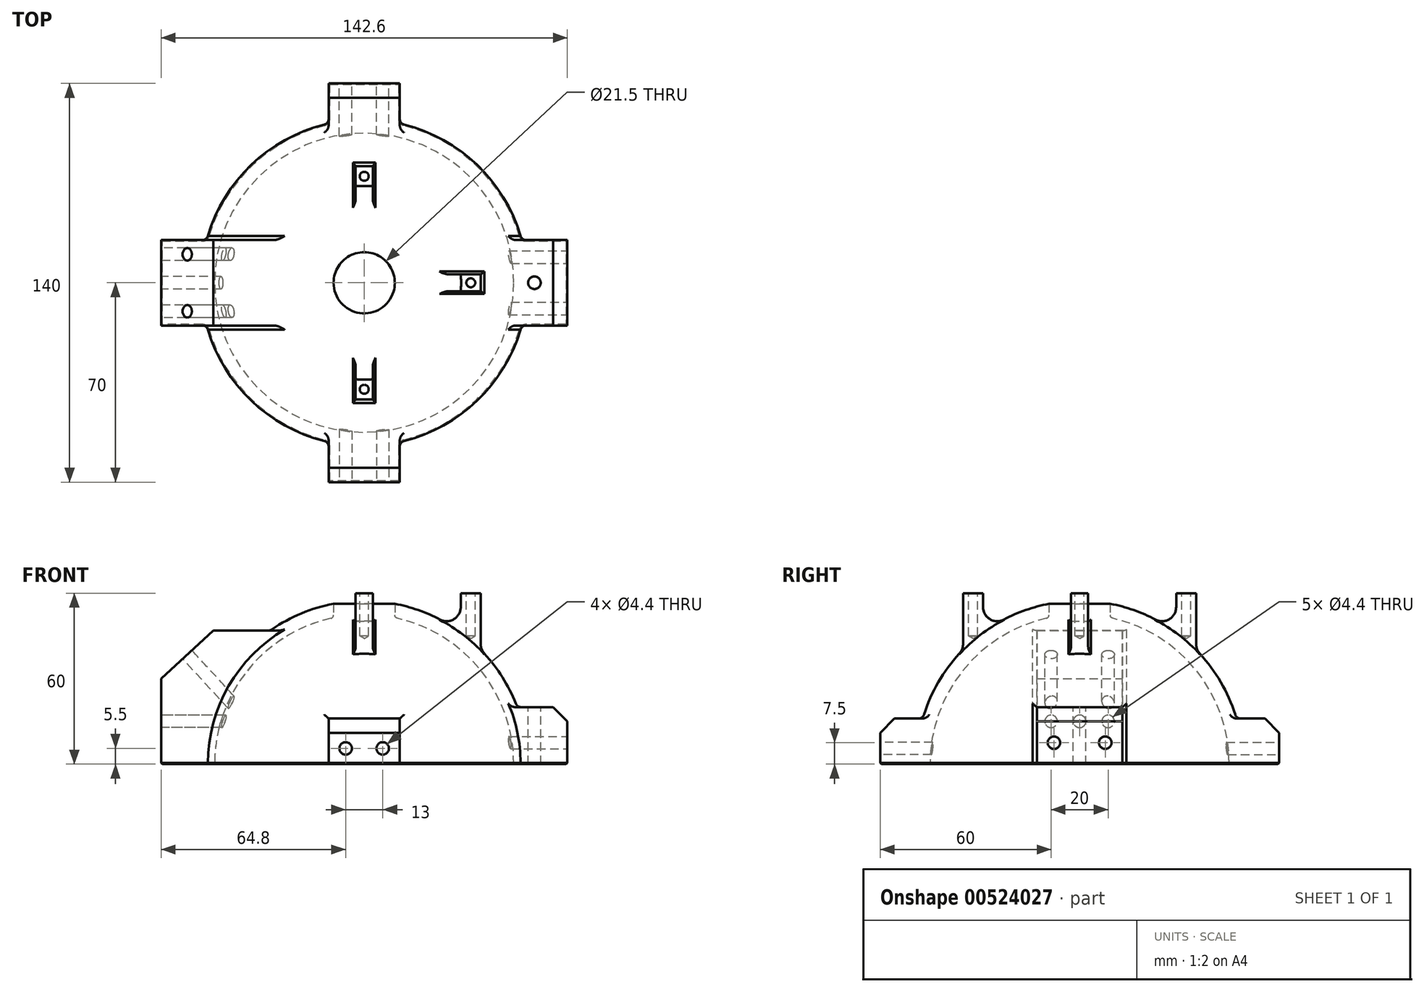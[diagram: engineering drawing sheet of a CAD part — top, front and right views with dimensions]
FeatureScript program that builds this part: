
annotation { "Feature Type Name" : "Feature", "Feature Type Description" : "" }
export const myFeature = defineFeature(function(context is Context, id is Id, definition is map)
    precondition{}
    {
        {
            var Q0;
            Q0=qCreatedBy(makeId("Front.planeOp"),FACE);
            var sketch = newSketch(context, id + "F0", { "sketchPlane" : qUnion([Q0])});
            skArc(sketch, "E0", {"start": v(52.5, 0) * mm, "mid": v(0, 52.5) * mm, "end": v(-52.5, 0) * mm});
            skLineSegment(sketch, "E1", {"start": v(-52.5, 0) * mm, "end": v(52.5, 0) * mm});
            skArc(sketch, "E2.0", {"start": v(57.3, 0) * mm, "mid": v(0, 57.3) * mm, "end": v(-57.3, 0) * mm});
            skLineSegment(sketch, "E3", {"start": v(-57.3, 0) * mm, "end": v(-52.5, 0) * mm});
            skLineSegment(sketch, "E4", {"start": v(52.5, 0) * mm, "end": v(57.3, 0) * mm});
            skLineSegment(sketch, "E5", {"start": v(-57.3, 0) * mm, "end": v(-71.3, 0) * mm});
            skLineSegment(sketch, "E6", {"start": v(-71.3, 0) * mm, "end": v(-71.3, 30) * mm});
            skLineSegment(sketch, "E7", {"start": v(-71.3, 30) * mm, "end": v(-52.9, 46.92) * mm});
            skLineSegment(sketch, "E8", {"start": v(-52.9, 46.92) * mm, "end": v(-32.9, 46.92) * mm});
            skLineSegment(sketch, "E9", {"start": v(0, 0) * mm, "end": v(0, 57.3) * mm});
            skLineSegment(sketch, "E10", {"start": v(-32.9, 46.92) * mm, "end": v(-23.56, 46.92) * mm});
            skLineSegment(sketch, "E11.bottom", {"start": v(10.75, 49.8) * mm, "end": v(-10.75, 49.8) * mm});
            skLineSegment(sketch, "E11.top", {"start": v(10.75, 64.8) * mm, "end": v(-10.75, 64.8) * mm});
            skLineSegment(sketch, "E11.left", {"start": v(10.75, 49.8) * mm, "end": v(10.75, 64.8) * mm});
            skLineSegment(sketch, "E11.right", {"start": v(-10.75, 49.8) * mm, "end": v(-10.75, 64.8) * mm});
            skPoint(sketch, "E11.middle", {"position": v(0, 57.3) * mm});
            skLineSegment(sketch, "E12", {"start": v(57.3, 0) * mm, "end": v(71.3, 0) * mm});
            skLineSegment(sketch, "E13", {"start": v(71.3, 0) * mm, "end": v(71.3, 20) * mm});
            skLineSegment(sketch, "E14", {"start": v(71.3, 20) * mm, "end": v(48.54, 20) * mm});
            skSolve(sketch);
        }
        {
            var Q0;
            {var subQ0=sQuery(id+"F0.wireOp",EDGE,"E4");Q0=makeQuery(id+"F0.imprint","IMPRINT",FACE,{"disambiguationData":[TD([[makeQuery(id+"F0.imprint","IMPRINT",EDGE,{"derivedFrom":subQ0}),1.0]])]});}
            var Q1;
            {var subQ0=sQuery(id+"F0.wireOp",EDGE,"E14");var subQ1=sQuery(id+"F0.wireOp",EDGE,"E0");var subQ2=makeQuery(id+"F0.imprint","INTERSECT",VERTEX,{"derivedFrom":[subQ1,subQ0]});Q1=makeQuery(id+"F0.imprint","IMPRINT",FACE,{"disambiguationData":[TD([[makeQuery(id+"F0.imprint","IMPRINT",EDGE,{"disambiguationData":[TD([[subQ2,-1.0]])],"derivedFrom":subQ1}),-1.0]])]});}
            var Q2;
            Q2=sQuery(id+"F0.wireOp",EDGE,"E9");
            revolve(context, id + "F1", {"entities" : qUnion([Q0, Q1]), "axis" : qUnion([Q2]), "revolveType" : RevolveType.FULL});
        }
        {
            var Q0;
            {var subQ0=sQuery(id+"F0.wireOp",EDGE,"E5");Q0=makeQuery(id+"F0.imprint","IMPRINT",FACE,{"disambiguationData":[TD([[makeQuery(id+"F0.imprint","IMPRINT",EDGE,{"derivedFrom":subQ0}),-1.0]])]});}
            var Q1;
            {var subQ0=sQuery(id+"F0.wireOp",EDGE,"E3");Q1=makeQuery(id+"F0.imprint","IMPRINT",FACE,{"disambiguationData":[TD([[makeQuery(id+"F0.imprint","IMPRINT",EDGE,{"derivedFrom":subQ0}),1.0]])]});}
            var Q2;
            {var subQ0=sQuery(id+"F0.wireOp",EDGE,"E4");Q2=makeQuery(id+"F0.imprint","IMPRINT",FACE,{"disambiguationData":[TD([[makeQuery(id+"F0.imprint","IMPRINT",EDGE,{"derivedFrom":subQ0}),1.0]])]});}
            var Q3;
            {var subQ0=sQuery(id+"F0.wireOp",EDGE,"E12");Q3=makeQuery(id+"F0.imprint","IMPRINT",FACE,{"disambiguationData":[TD([[makeQuery(id+"F0.imprint","IMPRINT",EDGE,{"derivedFrom":subQ0}),1.0]])]});}
            extrude(context, id + "F2", {"entities" : qUnion([Q0, Q1, Q2, Q3]), "operationType" : NewBodyOperationType.ADD, "endBound" : BoundingType.SYMMETRIC, "depth" : 30 * mm, "offsetDistance" : 25 * mm});
        }
        {
            var Q0;
            Q0=qCreatedBy(makeId("Right.planeOp"),FACE);
            var sketch = newSketch(context, id + "F3", { "sketchPlane" : qUnion([Q0])});
            skLineSegment(sketch, "E15.bottom", {"start": v(-70, 0) * mm, "end": v(70, 0) * mm});
            skLineSegment(sketch, "E15.top", {"start": v(-70, 16) * mm, "end": v(70, 16) * mm});
            skLineSegment(sketch, "E15.left", {"start": v(-70, 0) * mm, "end": v(-70, 16) * mm});
            skLineSegment(sketch, "E15.right", {"start": v(70, 0) * mm, "end": v(70, 16) * mm});
            skPoint(sketch, "E15.middle", {"position": v(0, 8) * mm});
            skArc(sketch, "E16", {"start": v(-10.75, 56.28) * mm, "mid": v(-44.15, 36.52) * mm, "end": v(-57.3, 0) * mm});
            skArc(sketch, "E17", {"start": v(57.3, 0) * mm, "mid": v(44.15, 36.52) * mm, "end": v(10.75, 56.28) * mm});
            skArc(sketch, "E18", {"start": v(-10.75, 51.39) * mm, "mid": v(-40.75, 33.1) * mm, "end": v(-52.5, 0) * mm});
            skArc(sketch, "E19", {"start": v(52.5, 0) * mm, "mid": v(40.75, 33.1) * mm, "end": v(10.75, 51.39) * mm});
            skSolve(sketch);
        }
        {
            var Q0;
            {var subQ0=sQuery(id+"F3.wireOp",EDGE,"E16");var subQ1=sQuery(id+"F3.wireOp",EDGE,"E15.bottom");var subQ2=makeQuery(id+"F3.imprint","INTERSECT",VERTEX,{"derivedFrom":[subQ1,subQ0]});Q0=makeQuery(id+"F3.imprint","IMPRINT",FACE,{"disambiguationData":[TD([[makeQuery(id+"F3.imprint","IMPRINT",EDGE,{"disambiguationData":[TD([[subQ2,-1.0]])],"derivedFrom":subQ1}),1.0]])]});}
            var Q1;
            {var subQ0=sQuery(id+"F3.wireOp",EDGE,"E15.left");Q1=makeQuery(id+"F3.imprint","IMPRINT",FACE,{"disambiguationData":[TD([[makeQuery(id+"F3.imprint","IMPRINT",EDGE,{"derivedFrom":subQ0}),-1.0]])]});}
            var Q2;
            {var subQ0=sQuery(id+"F3.wireOp",EDGE,"E17");var subQ1=sQuery(id+"F3.wireOp",EDGE,"E15.bottom");var subQ2=makeQuery(id+"F3.imprint","INTERSECT",VERTEX,{"derivedFrom":[subQ1,subQ0]});Q2=makeQuery(id+"F3.imprint","IMPRINT",FACE,{"disambiguationData":[TD([[makeQuery(id+"F3.imprint","IMPRINT",EDGE,{"disambiguationData":[TD([[subQ2,1.0]])],"derivedFrom":subQ1}),1.0]])]});}
            var Q3;
            {var subQ0=sQuery(id+"F3.wireOp",EDGE,"E15.right");Q3=makeQuery(id+"F3.imprint","IMPRINT",FACE,{"disambiguationData":[TD([[makeQuery(id+"F3.imprint","IMPRINT",EDGE,{"derivedFrom":subQ0}),1.0]])]});}
            extrude(context, id + "F4", {"entities" : qUnion([Q0, Q1, Q2, Q3]), "operationType" : NewBodyOperationType.ADD, "endBound" : BoundingType.SYMMETRIC, "depth" : 25 * mm, "offsetDistance" : 25 * mm});
        }
        {
            var Q0;
            Q0=makeQuery(id+"F4.opExtrude","SWEPT_EDGE",EDGE,{"disambiguationData":[OSD([sQuery(id+"F3.wireOp",EDGE,"E15.top"),sQuery(id+"F3.wireOp",EDGE,"E15.left")])]});
            var Q1;
            Q1=makeQuery(id+"F2.opExtrude","SWEPT_EDGE",EDGE,{"disambiguationData":[OSD([sQuery(id+"F0.wireOp",EDGE,"E13"),sQuery(id+"F0.wireOp",EDGE,"E14")])]});
            var Q2;
            Q2=makeQuery(id+"F4.opExtrude","SWEPT_EDGE",EDGE,{"disambiguationData":[OSD([sQuery(id+"F3.wireOp",EDGE,"E15.top"),sQuery(id+"F3.wireOp",EDGE,"E15.right")])]});
            chamfer(context, id + "F5", {"entities" : qUnion([Q0, Q1, Q2]), "width" : 5 * mm, "tangentPropagation" : true});
        }
        {
            var Q0;
            Q0=makeQuery(id+"F1.opRevolve","SWEPT_EDGE",EDGE,{"disambiguationData":[OSD([sQuery(id+"F0.wireOp",EDGE,"E0"),sQuery(id+"F0.wireOp",EDGE,"E11.left")])]});
            fillet(context, id + "F6", {"entities" : qUnion([Q0]), "radius" : 1.2 * mm, "tangentPropagation" : true, "allowEdgeOverflow" : false});
        }
        {
            var Q0;
            Q0=makeQuery(id+"F2.boolean.opBoolean","INTERSECT",EDGE,{"derivedFrom":[makeQuery(id+"F1.opRevolve","SWEPT_FACE",FACE,{"disambiguationData":[OSD([sQuery(id+"F0.wireOp",EDGE,"E2.0")])]}),makeQuery(id+"F2.opExtrude","CAP_FACE",FACE,{"disambiguationData":[OSD([sQuery(id+"F0.wireOp",EDGE,"E0"),sQuery(id+"F0.wireOp",EDGE,"E3"),sQuery(id+"F0.wireOp",EDGE,"E5"),sQuery(id+"F0.wireOp",EDGE,"E6"),sQuery(id+"F0.wireOp",EDGE,"E7"),sQuery(id+"F0.wireOp",EDGE,"E8"),sQuery(id+"F0.wireOp",EDGE,"E10")])],"isStart":false})]});
            var Q1;
            Q1=makeQuery(id+"F2.boolean.opBoolean","INTERSECT",EDGE,{"derivedFrom":[makeQuery(id+"F1.opRevolve","SWEPT_FACE",FACE,{"disambiguationData":[OSD([sQuery(id+"F0.wireOp",EDGE,"E2.0")])]}),makeQuery(id+"F2.opExtrude","CAP_FACE",FACE,{"disambiguationData":[OSD([sQuery(id+"F0.wireOp",EDGE,"E0"),sQuery(id+"F0.wireOp",EDGE,"E4"),sQuery(id+"F0.wireOp",EDGE,"E12"),sQuery(id+"F0.wireOp",EDGE,"E13"),sQuery(id+"F0.wireOp",EDGE,"E14")])],"isStart":false})]});
            var Q2;
            Q2=makeQuery(id+"F4.boolean.opBoolean","INTERSECT",EDGE,{"derivedFrom":[makeQuery(id+"F1.opRevolve","SWEPT_FACE",FACE,{"disambiguationData":[OSD([sQuery(id+"F0.wireOp",EDGE,"E2.0")])]}),makeQuery(id+"F4.opExtrude","CAP_FACE",FACE,{"disambiguationData":[OSD([sQuery(id+"F3.wireOp",EDGE,"E15.bottom"),sQuery(id+"F3.wireOp",EDGE,"E15.top"),sQuery(id+"F3.wireOp",EDGE,"E15.left"),sQuery(id+"F3.wireOp",EDGE,"E18")])],"isStart":false})]});
            var Q3;
            Q3=makeQuery(id+"F4.boolean.opBoolean","INTERSECT",EDGE,{"derivedFrom":[makeQuery(id+"F1.opRevolve","SWEPT_FACE",FACE,{"disambiguationData":[OSD([sQuery(id+"F0.wireOp",EDGE,"E2.0")])]}),makeQuery(id+"F4.opExtrude","CAP_FACE",FACE,{"disambiguationData":[OSD([sQuery(id+"F3.wireOp",EDGE,"E15.bottom"),sQuery(id+"F3.wireOp",EDGE,"E15.top"),sQuery(id+"F3.wireOp",EDGE,"E15.left"),sQuery(id+"F3.wireOp",EDGE,"E18")])],"isStart":true})]});
            var Q4;
            Q4=makeQuery(id+"F2.boolean.opBoolean","INTERSECT",EDGE,{"derivedFrom":[makeQuery(id+"F1.opRevolve","SWEPT_FACE",FACE,{"disambiguationData":[OSD([sQuery(id+"F0.wireOp",EDGE,"E2.0")])]}),makeQuery(id+"F2.opExtrude","CAP_FACE",FACE,{"disambiguationData":[OSD([sQuery(id+"F0.wireOp",EDGE,"E0"),sQuery(id+"F0.wireOp",EDGE,"E3"),sQuery(id+"F0.wireOp",EDGE,"E5"),sQuery(id+"F0.wireOp",EDGE,"E6"),sQuery(id+"F0.wireOp",EDGE,"E7"),sQuery(id+"F0.wireOp",EDGE,"E8"),sQuery(id+"F0.wireOp",EDGE,"E10")])],"isStart":true})]});
            var Q5;
            Q5=makeQuery(id+"F4.boolean.opBoolean","INTERSECT",EDGE,{"derivedFrom":[makeQuery(id+"F1.opRevolve","SWEPT_FACE",FACE,{"disambiguationData":[OSD([sQuery(id+"F0.wireOp",EDGE,"E2.0")])]}),makeQuery(id+"F4.opExtrude","CAP_FACE",FACE,{"disambiguationData":[OSD([sQuery(id+"F3.wireOp",EDGE,"E15.bottom"),sQuery(id+"F3.wireOp",EDGE,"E15.top"),sQuery(id+"F3.wireOp",EDGE,"E15.right"),sQuery(id+"F3.wireOp",EDGE,"E19")])],"isStart":true})]});
            var Q6;
            Q6=makeQuery(id+"F4.boolean.opBoolean","INTERSECT",EDGE,{"derivedFrom":[makeQuery(id+"F1.opRevolve","SWEPT_FACE",FACE,{"disambiguationData":[OSD([sQuery(id+"F0.wireOp",EDGE,"E2.0")])]}),makeQuery(id+"F4.opExtrude","CAP_FACE",FACE,{"disambiguationData":[OSD([sQuery(id+"F3.wireOp",EDGE,"E15.bottom"),sQuery(id+"F3.wireOp",EDGE,"E15.top"),sQuery(id+"F3.wireOp",EDGE,"E15.right"),sQuery(id+"F3.wireOp",EDGE,"E19")])],"isStart":false})]});
            var Q7;
            Q7=makeQuery(id+"F2.boolean.opBoolean","INTERSECT",EDGE,{"derivedFrom":[makeQuery(id+"F1.opRevolve","SWEPT_FACE",FACE,{"disambiguationData":[OSD([sQuery(id+"F0.wireOp",EDGE,"E2.0")])]}),makeQuery(id+"F2.opExtrude","SWEPT_FACE",FACE,{"disambiguationData":[OSD([sQuery(id+"F0.wireOp",EDGE,"E8"),sQuery(id+"F0.wireOp",EDGE,"E10")])]})]});
            var Q8;
            {var subQ0=sQuery(id+"F3.wireOp",EDGE,"E15.top");var subQ1=makeQuery(id+"F3.imprint","INTERSECT",VERTEX,{"derivedFrom":[subQ0,sQuery(id+"F3.wireOp",EDGE,"E16")]});Q8=makeQuery(id+"F4.boolean.opBoolean","INTERSECT",EDGE,{"derivedFrom":[makeQuery(id+"F1.opRevolve","SWEPT_FACE",FACE,{"disambiguationData":[OSD([sQuery(id+"F0.wireOp",EDGE,"E2.0")])]}),makeQuery(id+"F4.opExtrude","SWEPT_FACE",FACE,{"disambiguationData":[OSD([subQ0]),TDD([makeQuery(id+"F3.imprint","IMPRINT",EDGE,{"disambiguationData":[TD([[makeQuery(id+"F3.imprint","INTERSECT",VERTEX,{"derivedFrom":[subQ0,sQuery(id+"F3.wireOp",EDGE,"E15.left")]}),-1.0]])],"derivedFrom":subQ0}),makeQuery(id+"F3.imprint","IMPRINT",EDGE,{"disambiguationData":[TD([[subQ1,-1.0]])],"derivedFrom":subQ0})])]})]});}
            var Q9;
            Q9=makeQuery(id+"F2.boolean.opBoolean","INTERSECT",EDGE,{"derivedFrom":[makeQuery(id+"F1.opRevolve","SWEPT_FACE",FACE,{"disambiguationData":[OSD([sQuery(id+"F0.wireOp",EDGE,"E2.0")])]}),makeQuery(id+"F2.opExtrude","CAP_FACE",FACE,{"disambiguationData":[OSD([sQuery(id+"F0.wireOp",EDGE,"E0"),sQuery(id+"F0.wireOp",EDGE,"E4"),sQuery(id+"F0.wireOp",EDGE,"E12"),sQuery(id+"F0.wireOp",EDGE,"E13"),sQuery(id+"F0.wireOp",EDGE,"E14")])],"isStart":true})]});
            var Q10;
            Q10=makeQuery(id+"F2.boolean.opBoolean","INTERSECT",EDGE,{"derivedFrom":[makeQuery(id+"F1.opRevolve","SWEPT_FACE",FACE,{"disambiguationData":[OSD([sQuery(id+"F0.wireOp",EDGE,"E2.0")])]}),makeQuery(id+"F2.opExtrude","SWEPT_FACE",FACE,{"disambiguationData":[OSD([sQuery(id+"F0.wireOp",EDGE,"E14")])]})]});
            var Q11;
            {var subQ0=sQuery(id+"F3.wireOp",EDGE,"E15.top");Q11=makeQuery(id+"F4.boolean.opBoolean","INTERSECT",EDGE,{"derivedFrom":[makeQuery(id+"F1.opRevolve","SWEPT_FACE",FACE,{"disambiguationData":[OSD([sQuery(id+"F0.wireOp",EDGE,"E2.0")])]}),makeQuery(id+"F4.opExtrude","SWEPT_FACE",FACE,{"disambiguationData":[OSD([subQ0]),TDD([makeQuery(id+"F3.imprint","IMPRINT",EDGE,{"disambiguationData":[TD([[makeQuery(id+"F3.imprint","INTERSECT",VERTEX,{"derivedFrom":[subQ0,sQuery(id+"F3.wireOp",EDGE,"E19")]}),-1.0]])],"derivedFrom":subQ0}),makeQuery(id+"F3.imprint","IMPRINT",EDGE,{"disambiguationData":[TD([[makeQuery(id+"F3.imprint","INTERSECT",VERTEX,{"derivedFrom":[subQ0,sQuery(id+"F3.wireOp",EDGE,"E15.right")]}),1.0]])],"derivedFrom":subQ0})])]})]});}
            fillet(context, id + "F7", {"entities" : qUnion([Q0, Q1, Q2, Q3, Q4, Q5, Q6, Q7, Q8, Q9, Q10, Q11]), "radius" : 2 * mm, "tangentPropagation" : true, "allowEdgeOverflow" : false});
        }
        {
            var Q0;
            Q0=makeQuery(id+"F2.opExtrude","SWEPT_FACE",FACE,{"disambiguationData":[OSD([sQuery(id+"F0.wireOp",EDGE,"E6")])]});
            var sketch = newSketch(context, id + "F8", { "sketchPlane" : qUnion([Q0])});
            skPoint(sketch, "E20", {"position": v(-10, 15) * mm});
            skPoint(sketch, "E20.positionSnap0", {"position": v(-15, 15) * mm});
            skPoint(sketch, "E21", {"position": v(10, 15) * mm});
            skPoint(sketch, "E22", {"position": v(0, 15) * mm});
            skSolve(sketch);
        }
        {
            var Q0;
            Q0=makeQuery(id+"F2.opExtrude","SWEPT_FACE",FACE,{"disambiguationData":[OSD([sQuery(id+"F0.wireOp",EDGE,"E7")])]});
            var sketch = newSketch(context, id + "F9", { "sketchPlane" : qUnion([Q0])});
            skPoint(sketch, "E23", {"position": v(-19.7, 10) * mm});
            skPoint(sketch, "E23.positionSnap0", {"position": v(-19.7, 15) * mm});
            skPoint(sketch, "E24", {"position": v(-19.7, -10) * mm});
            skPoint(sketch, "E25", {"position": v(-19.7, 0) * mm});
            skSolve(sketch);
        }
        {
            var Q0;
            Q0=makeQuery(id+"F4.opExtrude","SWEPT_FACE",FACE,{"disambiguationData":[OSD([sQuery(id+"F3.wireOp",EDGE,"E15.right")])]});
            var sketch = newSketch(context, id + "F10", { "sketchPlane" : qUnion([Q0])});
            skPoint(sketch, "E26", {"position": v(-6.5, 5.5) * mm});
            skPoint(sketch, "E26.positionSnap0", {"position": v(0, 11) * mm});
            skPoint(sketch, "E26.positionSnap1", {"position": v(12.5, 5.5) * mm});
            skPoint(sketch, "E27", {"position": v(6.5, 5.5) * mm});
            skSolve(sketch);
        }
        {
            var Q0;
            Q0=makeQuery(id+"F4.opExtrude","SWEPT_FACE",FACE,{"disambiguationData":[OSD([sQuery(id+"F3.wireOp",EDGE,"E15.left")])]});
            var sketch = newSketch(context, id + "F11", { "sketchPlane" : qUnion([Q0])});
            skPoint(sketch, "E28", {"position": v(6.5, 5.5) * mm});
            skPoint(sketch, "E28.positionSnap0", {"position": v(12.5, 5.5) * mm});
            skPoint(sketch, "E28.positionSnap1", {"position": v(0, 11) * mm});
            skPoint(sketch, "E29", {"position": v(-6.5, 5.5) * mm});
            skSolve(sketch);
        }
        {
            var Q0;
            Q0=makeQuery(id+"F2.opExtrude","SWEPT_FACE",FACE,{"disambiguationData":[OSD([sQuery(id+"F0.wireOp",EDGE,"E13")])]});
            var sketch = newSketch(context, id + "F12", { "sketchPlane" : qUnion([Q0])});
            skPoint(sketch, "E30", {"position": v(-9, 7.5) * mm});
            skPoint(sketch, "E30.positionSnap0", {"position": v(-15, 7.5) * mm});
            skPoint(sketch, "E31", {"position": v(9, 7.5) * mm});
            skPoint(sketch, "E31.positionSnap0", {"position": v(15, 7.5) * mm});
            skSolve(sketch);
        }
        {
            var Q0;
            Q0=makeQuery(id+"F2.opExtrude","SWEPT_FACE",FACE,{"disambiguationData":[OSD([sQuery(id+"F0.wireOp",EDGE,"E14")])]});
            var sketch = newSketch(context, id + "F13", { "sketchPlane" : qUnion([Q0])});
            skPoint(sketch, "E32", {"position": v(59.74, 0) * mm});
            skPoint(sketch, "E32.positionSnap0", {"position": v(59.74, 15) * mm});
            skPoint(sketch, "E32.positionSnap1", {"position": v(66.3, 0) * mm});
            skSolve(sketch);
        }
        {
            var Q0;
            Q0=sQuery(id+"F9.wireOp",VERTEX,"E23");
            var Q1;
            Q1=sQuery(id+"F9.wireOp",VERTEX,"E24");
            var Q2;
            Q2=sQuery(id+"F8.wireOp",VERTEX,"E20");
            var Q3;
            Q3=sQuery(id+"F8.wireOp",VERTEX,"E22");
            var Q4;
            Q4=sQuery(id+"F8.wireOp",VERTEX,"E21");
            var Q5;
            Q5=sQuery(id+"F11.wireOp",VERTEX,"E28");
            var Q6;
            Q6=sQuery(id+"F10.wireOp",VERTEX,"E26");
            var Q7;
            Q7=sQuery(id+"F12.wireOp",VERTEX,"E30");
            var Q8;
            Q8=sQuery(id+"F12.wireOp",VERTEX,"E31");
            var Q9;
            Q9=sQuery(id+"F13.wireOp",VERTEX,"E32");
            var Q10;
            Q10=sQuery(id+"F10.wireOp",VERTEX,"E27");
            var Q11;
            Q11=sQuery(id+"F11.wireOp",VERTEX,"E29");
            var Q12;
            Q12=makeQuery(id+"F1.opRevolve","SWEPT_BODY",BODY,{"disambiguationData":[OSD([sQuery(id+"F0.wireOp",EDGE,"E0"),sQuery(id+"F0.wireOp",EDGE,"E2.0"),sQuery(id+"F0.wireOp",EDGE,"E4"),sQuery(id+"F0.wireOp",EDGE,"E11.left")])]});
            hole(context, id + "F14", {"style" : HoleStyle.SIMPLE, "endStyle" : HoleEndStyle.BLIND, "standardTappedOrClearance" : lookupTablePath({ "standard" : "ISO", "fit" : "Normal", "size" : "M4", "type" : "Clearance" }), "standardBlindInLast" : lookupTablePath({ "fit" : "Standard", "standard" : "ISO", "size" : "M4", "type" : "Clearance" }), "holeDiameter" : 4.4 * mm, "holeDepth" : 40 * mm, "isTappedThrough" : true, "tappedDepth" : 12 * mm, "tapClearance" : 3, "locations" : qUnion([Q0, Q1, Q2, Q3, Q4, Q5, Q6, Q7, Q8, Q9, Q10, Q11]), "scope" : qUnion([Q12])});
        }
        {
            var Q0;
            {var subQ0=sQuery(id+"F3.wireOp",EDGE,"E15.bottom");var subQ1=makeQuery(id+"F3.imprint","INTERSECT",VERTEX,{"derivedFrom":[subQ0,sQuery(id+"F3.wireOp",EDGE,"E17")]});var subQ2=makeQuery(id+"F3.imprint","INTERSECT",VERTEX,{"derivedFrom":[subQ0,sQuery(id+"F3.wireOp",EDGE,"E16")]});var subQ3=sQuery(id+"F3.wireOp",EDGE,"E18");var subQ4=sQuery(id+"F3.wireOp",EDGE,"E15.left");var subQ5=sQuery(id+"F0.wireOp",EDGE,"E4");Q0=makeQuery(id+"F7.opFillet","BLEND_EDGE",EDGE,{"blendedFrom":[makeQuery(id+"F4.boolean.opBoolean","INTERSECT",EDGE,{"derivedFrom":[makeQuery(id+"F1.opRevolve","SWEPT_FACE",FACE,{"disambiguationData":[OSD([sQuery(id+"F0.wireOp",EDGE,"E2.0")])]}),makeQuery(id+"F4.opExtrude","CAP_FACE",FACE,{"disambiguationData":[OSD([subQ0,sQuery(id+"F3.wireOp",EDGE,"E15.top"),subQ4,subQ3])],"isStart":false})]}),makeQuery(id+"F4.boolean.opBoolean","MERGE",FACE,{"derivedFrom":[makeQuery(id+"F2.boolean.opBoolean","MERGE",FACE,{"derivedFrom":[makeQuery(id+"F1.opRevolve","SWEPT_FACE",FACE,{"disambiguationData":[OSD([subQ5])]}),makeQuery(id+"F2.opExtrude","SWEPT_FACE",FACE,{"disambiguationData":[OSD([sQuery(id+"F0.wireOp",EDGE,"E3"),sQuery(id+"F0.wireOp",EDGE,"E5")])]}),makeQuery(id+"F2.opExtrude","SWEPT_FACE",FACE,{"disambiguationData":[OSD([subQ5,sQuery(id+"F0.wireOp",EDGE,"E12")])]})]}),makeQuery(id+"F4.opExtrude","SWEPT_FACE",FACE,{"disambiguationData":[OSD([subQ0]),TDD([makeQuery(id+"F3.imprint","IMPRINT",EDGE,{"disambiguationData":[TD([[makeQuery(id+"F3.imprint","INTERSECT",VERTEX,{"derivedFrom":[subQ0,subQ4]}),-1.0]])],"derivedFrom":subQ0}),makeQuery(id+"F3.imprint","IMPRINT",EDGE,{"disambiguationData":[TD([[subQ2,-1.0]])],"derivedFrom":subQ0})])]}),makeQuery(id+"F4.opExtrude","SWEPT_FACE",FACE,{"disambiguationData":[OSD([subQ0]),TDD([makeQuery(id+"F3.imprint","IMPRINT",EDGE,{"disambiguationData":[TD([[subQ1,1.0]])],"derivedFrom":subQ0}),makeQuery(id+"F3.imprint","IMPRINT",EDGE,{"disambiguationData":[TD([[makeQuery(id+"F3.imprint","INTERSECT",VERTEX,{"derivedFrom":[subQ0,sQuery(id+"F3.wireOp",EDGE,"E15.right")]}),1.0]])],"derivedFrom":subQ0})])]})]})],"blendedInto":[makeQuery(id+"F4.boolean.opBoolean","MERGE",FACE,{"derivedFrom":[makeQuery(id+"F2.boolean.opBoolean","MERGE",FACE,{"derivedFrom":[makeQuery(id+"F1.opRevolve","SWEPT_FACE",FACE,{"disambiguationData":[OSD([subQ5])]}),makeQuery(id+"F2.opExtrude","SWEPT_FACE",FACE,{"disambiguationData":[OSD([sQuery(id+"F0.wireOp",EDGE,"E3"),sQuery(id+"F0.wireOp",EDGE,"E5")])]}),makeQuery(id+"F2.opExtrude","SWEPT_FACE",FACE,{"disambiguationData":[OSD([subQ5,sQuery(id+"F0.wireOp",EDGE,"E12")])]})]}),makeQuery(id+"F4.opExtrude","SWEPT_FACE",FACE,{"disambiguationData":[OSD([subQ0]),TDD([makeQuery(id+"F3.imprint","IMPRINT",EDGE,{"disambiguationData":[TD([[makeQuery(id+"F3.imprint","INTERSECT",VERTEX,{"derivedFrom":[subQ0,subQ4]}),-1.0]])],"derivedFrom":subQ0}),makeQuery(id+"F3.imprint","IMPRINT",EDGE,{"disambiguationData":[TD([[subQ2,-1.0]])],"derivedFrom":subQ0})])]}),makeQuery(id+"F4.opExtrude","SWEPT_FACE",FACE,{"disambiguationData":[OSD([subQ0]),TDD([makeQuery(id+"F3.imprint","IMPRINT",EDGE,{"disambiguationData":[TD([[subQ1,1.0]])],"derivedFrom":subQ0}),makeQuery(id+"F3.imprint","IMPRINT",EDGE,{"disambiguationData":[TD([[makeQuery(id+"F3.imprint","INTERSECT",VERTEX,{"derivedFrom":[subQ0,sQuery(id+"F3.wireOp",EDGE,"E15.right")]}),1.0]])],"derivedFrom":subQ0})])]})]})]});}
            var Q1;
            {var subQ0=sQuery(id+"F3.wireOp",EDGE,"E15.bottom");var subQ1=makeQuery(id+"F3.imprint","INTERSECT",VERTEX,{"derivedFrom":[subQ0,sQuery(id+"F3.wireOp",EDGE,"E17")]});var subQ2=makeQuery(id+"F3.imprint","INTERSECT",VERTEX,{"derivedFrom":[subQ0,sQuery(id+"F3.wireOp",EDGE,"E16")]});var subQ3=sQuery(id+"F3.wireOp",EDGE,"E18");var subQ4=sQuery(id+"F3.wireOp",EDGE,"E15.left");var subQ5=sQuery(id+"F0.wireOp",EDGE,"E4");Q1=makeQuery(id+"F7.opFillet","BLEND_EDGE",EDGE,{"blendedFrom":[makeQuery(id+"F4.boolean.opBoolean","INTERSECT",EDGE,{"derivedFrom":[makeQuery(id+"F1.opRevolve","SWEPT_FACE",FACE,{"disambiguationData":[OSD([sQuery(id+"F0.wireOp",EDGE,"E2.0")])]}),makeQuery(id+"F4.opExtrude","CAP_FACE",FACE,{"disambiguationData":[OSD([subQ0,sQuery(id+"F3.wireOp",EDGE,"E15.top"),subQ4,subQ3])],"isStart":true})]}),makeQuery(id+"F4.boolean.opBoolean","MERGE",FACE,{"derivedFrom":[makeQuery(id+"F2.boolean.opBoolean","MERGE",FACE,{"derivedFrom":[makeQuery(id+"F1.opRevolve","SWEPT_FACE",FACE,{"disambiguationData":[OSD([subQ5])]}),makeQuery(id+"F2.opExtrude","SWEPT_FACE",FACE,{"disambiguationData":[OSD([sQuery(id+"F0.wireOp",EDGE,"E3"),sQuery(id+"F0.wireOp",EDGE,"E5")])]}),makeQuery(id+"F2.opExtrude","SWEPT_FACE",FACE,{"disambiguationData":[OSD([subQ5,sQuery(id+"F0.wireOp",EDGE,"E12")])]})]}),makeQuery(id+"F4.opExtrude","SWEPT_FACE",FACE,{"disambiguationData":[OSD([subQ0]),TDD([makeQuery(id+"F3.imprint","IMPRINT",EDGE,{"disambiguationData":[TD([[makeQuery(id+"F3.imprint","INTERSECT",VERTEX,{"derivedFrom":[subQ0,subQ4]}),-1.0]])],"derivedFrom":subQ0}),makeQuery(id+"F3.imprint","IMPRINT",EDGE,{"disambiguationData":[TD([[subQ2,-1.0]])],"derivedFrom":subQ0})])]}),makeQuery(id+"F4.opExtrude","SWEPT_FACE",FACE,{"disambiguationData":[OSD([subQ0]),TDD([makeQuery(id+"F3.imprint","IMPRINT",EDGE,{"disambiguationData":[TD([[subQ1,1.0]])],"derivedFrom":subQ0}),makeQuery(id+"F3.imprint","IMPRINT",EDGE,{"disambiguationData":[TD([[makeQuery(id+"F3.imprint","INTERSECT",VERTEX,{"derivedFrom":[subQ0,sQuery(id+"F3.wireOp",EDGE,"E15.right")]}),1.0]])],"derivedFrom":subQ0})])]})]})],"blendedInto":[makeQuery(id+"F4.boolean.opBoolean","MERGE",FACE,{"derivedFrom":[makeQuery(id+"F2.boolean.opBoolean","MERGE",FACE,{"derivedFrom":[makeQuery(id+"F1.opRevolve","SWEPT_FACE",FACE,{"disambiguationData":[OSD([subQ5])]}),makeQuery(id+"F2.opExtrude","SWEPT_FACE",FACE,{"disambiguationData":[OSD([sQuery(id+"F0.wireOp",EDGE,"E3"),sQuery(id+"F0.wireOp",EDGE,"E5")])]}),makeQuery(id+"F2.opExtrude","SWEPT_FACE",FACE,{"disambiguationData":[OSD([subQ5,sQuery(id+"F0.wireOp",EDGE,"E12")])]})]}),makeQuery(id+"F4.opExtrude","SWEPT_FACE",FACE,{"disambiguationData":[OSD([subQ0]),TDD([makeQuery(id+"F3.imprint","IMPRINT",EDGE,{"disambiguationData":[TD([[makeQuery(id+"F3.imprint","INTERSECT",VERTEX,{"derivedFrom":[subQ0,subQ4]}),-1.0]])],"derivedFrom":subQ0}),makeQuery(id+"F3.imprint","IMPRINT",EDGE,{"disambiguationData":[TD([[subQ2,-1.0]])],"derivedFrom":subQ0})])]}),makeQuery(id+"F4.opExtrude","SWEPT_FACE",FACE,{"disambiguationData":[OSD([subQ0]),TDD([makeQuery(id+"F3.imprint","IMPRINT",EDGE,{"disambiguationData":[TD([[subQ1,1.0]])],"derivedFrom":subQ0}),makeQuery(id+"F3.imprint","IMPRINT",EDGE,{"disambiguationData":[TD([[makeQuery(id+"F3.imprint","INTERSECT",VERTEX,{"derivedFrom":[subQ0,sQuery(id+"F3.wireOp",EDGE,"E15.right")]}),1.0]])],"derivedFrom":subQ0})])]})]})]});}
            var Q2;
            {var subQ0=sQuery(id+"F3.wireOp",EDGE,"E15.bottom");var subQ1=makeQuery(id+"F3.imprint","INTERSECT",VERTEX,{"derivedFrom":[subQ0,sQuery(id+"F3.wireOp",EDGE,"E17")]});var subQ2=makeQuery(id+"F3.imprint","INTERSECT",VERTEX,{"derivedFrom":[subQ0,sQuery(id+"F3.wireOp",EDGE,"E16")]});var subQ3=sQuery(id+"F0.wireOp",EDGE,"E12");var subQ4=sQuery(id+"F0.wireOp",EDGE,"E4");Q2=makeQuery(id+"F7.opFillet","BLEND_EDGE",EDGE,{"blendedFrom":[makeQuery(id+"F2.boolean.opBoolean","INTERSECT",EDGE,{"derivedFrom":[makeQuery(id+"F1.opRevolve","SWEPT_FACE",FACE,{"disambiguationData":[OSD([sQuery(id+"F0.wireOp",EDGE,"E2.0")])]}),makeQuery(id+"F2.opExtrude","CAP_FACE",FACE,{"disambiguationData":[OSD([sQuery(id+"F0.wireOp",EDGE,"E0"),subQ4,subQ3,sQuery(id+"F0.wireOp",EDGE,"E13"),sQuery(id+"F0.wireOp",EDGE,"E14")])],"isStart":true})]}),makeQuery(id+"F4.boolean.opBoolean","MERGE",FACE,{"derivedFrom":[makeQuery(id+"F2.boolean.opBoolean","MERGE",FACE,{"derivedFrom":[makeQuery(id+"F1.opRevolve","SWEPT_FACE",FACE,{"disambiguationData":[OSD([subQ4])]}),makeQuery(id+"F2.opExtrude","SWEPT_FACE",FACE,{"disambiguationData":[OSD([sQuery(id+"F0.wireOp",EDGE,"E3"),sQuery(id+"F0.wireOp",EDGE,"E5")])]}),makeQuery(id+"F2.opExtrude","SWEPT_FACE",FACE,{"disambiguationData":[OSD([subQ4,subQ3])]})]}),makeQuery(id+"F4.opExtrude","SWEPT_FACE",FACE,{"disambiguationData":[OSD([subQ0]),TDD([makeQuery(id+"F3.imprint","IMPRINT",EDGE,{"disambiguationData":[TD([[makeQuery(id+"F3.imprint","INTERSECT",VERTEX,{"derivedFrom":[subQ0,sQuery(id+"F3.wireOp",EDGE,"E15.left")]}),-1.0]])],"derivedFrom":subQ0}),makeQuery(id+"F3.imprint","IMPRINT",EDGE,{"disambiguationData":[TD([[subQ2,-1.0]])],"derivedFrom":subQ0})])]}),makeQuery(id+"F4.opExtrude","SWEPT_FACE",FACE,{"disambiguationData":[OSD([subQ0]),TDD([makeQuery(id+"F3.imprint","IMPRINT",EDGE,{"disambiguationData":[TD([[subQ1,1.0]])],"derivedFrom":subQ0}),makeQuery(id+"F3.imprint","IMPRINT",EDGE,{"disambiguationData":[TD([[makeQuery(id+"F3.imprint","INTERSECT",VERTEX,{"derivedFrom":[subQ0,sQuery(id+"F3.wireOp",EDGE,"E15.right")]}),1.0]])],"derivedFrom":subQ0})])]})]})],"blendedInto":[makeQuery(id+"F4.boolean.opBoolean","MERGE",FACE,{"derivedFrom":[makeQuery(id+"F2.boolean.opBoolean","MERGE",FACE,{"derivedFrom":[makeQuery(id+"F1.opRevolve","SWEPT_FACE",FACE,{"disambiguationData":[OSD([subQ4])]}),makeQuery(id+"F2.opExtrude","SWEPT_FACE",FACE,{"disambiguationData":[OSD([sQuery(id+"F0.wireOp",EDGE,"E3"),sQuery(id+"F0.wireOp",EDGE,"E5")])]}),makeQuery(id+"F2.opExtrude","SWEPT_FACE",FACE,{"disambiguationData":[OSD([subQ4,subQ3])]})]}),makeQuery(id+"F4.opExtrude","SWEPT_FACE",FACE,{"disambiguationData":[OSD([subQ0]),TDD([makeQuery(id+"F3.imprint","IMPRINT",EDGE,{"disambiguationData":[TD([[makeQuery(id+"F3.imprint","INTERSECT",VERTEX,{"derivedFrom":[subQ0,sQuery(id+"F3.wireOp",EDGE,"E15.left")]}),-1.0]])],"derivedFrom":subQ0}),makeQuery(id+"F3.imprint","IMPRINT",EDGE,{"disambiguationData":[TD([[subQ2,-1.0]])],"derivedFrom":subQ0})])]}),makeQuery(id+"F4.opExtrude","SWEPT_FACE",FACE,{"disambiguationData":[OSD([subQ0]),TDD([makeQuery(id+"F3.imprint","IMPRINT",EDGE,{"disambiguationData":[TD([[subQ1,1.0]])],"derivedFrom":subQ0}),makeQuery(id+"F3.imprint","IMPRINT",EDGE,{"disambiguationData":[TD([[makeQuery(id+"F3.imprint","INTERSECT",VERTEX,{"derivedFrom":[subQ0,sQuery(id+"F3.wireOp",EDGE,"E15.right")]}),1.0]])],"derivedFrom":subQ0})])]})]})]});}
            var Q3;
            {var subQ0=sQuery(id+"F3.wireOp",EDGE,"E15.right");var subQ1=sQuery(id+"F3.wireOp",EDGE,"E15.bottom");var subQ2=makeQuery(id+"F3.imprint","INTERSECT",VERTEX,{"derivedFrom":[subQ1,sQuery(id+"F3.wireOp",EDGE,"E17")]});var subQ3=sQuery(id+"F3.wireOp",EDGE,"E19");var subQ4=makeQuery(id+"F3.imprint","INTERSECT",VERTEX,{"derivedFrom":[subQ1,sQuery(id+"F3.wireOp",EDGE,"E16")]});var subQ5=sQuery(id+"F0.wireOp",EDGE,"E4");Q3=makeQuery(id+"F7.opFillet","BLEND_EDGE",EDGE,{"blendedFrom":[makeQuery(id+"F4.boolean.opBoolean","INTERSECT",EDGE,{"derivedFrom":[makeQuery(id+"F1.opRevolve","SWEPT_FACE",FACE,{"disambiguationData":[OSD([sQuery(id+"F0.wireOp",EDGE,"E2.0")])]}),makeQuery(id+"F4.opExtrude","CAP_FACE",FACE,{"disambiguationData":[OSD([subQ1,sQuery(id+"F3.wireOp",EDGE,"E15.top"),subQ0,subQ3])],"isStart":true})]}),makeQuery(id+"F4.boolean.opBoolean","MERGE",FACE,{"derivedFrom":[makeQuery(id+"F2.boolean.opBoolean","MERGE",FACE,{"derivedFrom":[makeQuery(id+"F1.opRevolve","SWEPT_FACE",FACE,{"disambiguationData":[OSD([subQ5])]}),makeQuery(id+"F2.opExtrude","SWEPT_FACE",FACE,{"disambiguationData":[OSD([sQuery(id+"F0.wireOp",EDGE,"E3"),sQuery(id+"F0.wireOp",EDGE,"E5")])]}),makeQuery(id+"F2.opExtrude","SWEPT_FACE",FACE,{"disambiguationData":[OSD([subQ5,sQuery(id+"F0.wireOp",EDGE,"E12")])]})]}),makeQuery(id+"F4.opExtrude","SWEPT_FACE",FACE,{"disambiguationData":[OSD([subQ1]),TDD([makeQuery(id+"F3.imprint","IMPRINT",EDGE,{"disambiguationData":[TD([[makeQuery(id+"F3.imprint","INTERSECT",VERTEX,{"derivedFrom":[subQ1,sQuery(id+"F3.wireOp",EDGE,"E15.left")]}),-1.0]])],"derivedFrom":subQ1}),makeQuery(id+"F3.imprint","IMPRINT",EDGE,{"disambiguationData":[TD([[subQ4,-1.0]])],"derivedFrom":subQ1})])]}),makeQuery(id+"F4.opExtrude","SWEPT_FACE",FACE,{"disambiguationData":[OSD([subQ1]),TDD([makeQuery(id+"F3.imprint","IMPRINT",EDGE,{"disambiguationData":[TD([[subQ2,1.0]])],"derivedFrom":subQ1}),makeQuery(id+"F3.imprint","IMPRINT",EDGE,{"disambiguationData":[TD([[makeQuery(id+"F3.imprint","INTERSECT",VERTEX,{"derivedFrom":[subQ1,subQ0]}),1.0]])],"derivedFrom":subQ1})])]})]})],"blendedInto":[makeQuery(id+"F4.boolean.opBoolean","MERGE",FACE,{"derivedFrom":[makeQuery(id+"F2.boolean.opBoolean","MERGE",FACE,{"derivedFrom":[makeQuery(id+"F1.opRevolve","SWEPT_FACE",FACE,{"disambiguationData":[OSD([subQ5])]}),makeQuery(id+"F2.opExtrude","SWEPT_FACE",FACE,{"disambiguationData":[OSD([sQuery(id+"F0.wireOp",EDGE,"E3"),sQuery(id+"F0.wireOp",EDGE,"E5")])]}),makeQuery(id+"F2.opExtrude","SWEPT_FACE",FACE,{"disambiguationData":[OSD([subQ5,sQuery(id+"F0.wireOp",EDGE,"E12")])]})]}),makeQuery(id+"F4.opExtrude","SWEPT_FACE",FACE,{"disambiguationData":[OSD([subQ1]),TDD([makeQuery(id+"F3.imprint","IMPRINT",EDGE,{"disambiguationData":[TD([[makeQuery(id+"F3.imprint","INTERSECT",VERTEX,{"derivedFrom":[subQ1,sQuery(id+"F3.wireOp",EDGE,"E15.left")]}),-1.0]])],"derivedFrom":subQ1}),makeQuery(id+"F3.imprint","IMPRINT",EDGE,{"disambiguationData":[TD([[subQ4,-1.0]])],"derivedFrom":subQ1})])]}),makeQuery(id+"F4.opExtrude","SWEPT_FACE",FACE,{"disambiguationData":[OSD([subQ1]),TDD([makeQuery(id+"F3.imprint","IMPRINT",EDGE,{"disambiguationData":[TD([[subQ2,1.0]])],"derivedFrom":subQ1}),makeQuery(id+"F3.imprint","IMPRINT",EDGE,{"disambiguationData":[TD([[makeQuery(id+"F3.imprint","INTERSECT",VERTEX,{"derivedFrom":[subQ1,subQ0]}),1.0]])],"derivedFrom":subQ1})])]})]})]});}
            var Q4;
            Q4=makeQuery(id+"F2.opExtrude","SWEPT_EDGE",EDGE,{"disambiguationData":[OSD([sQuery(id+"F0.wireOp",EDGE,"E5"),sQuery(id+"F0.wireOp",EDGE,"E6")])]});
            var Q5;
            Q5=makeQuery(id+"F4.opExtrude","SWEPT_EDGE",EDGE,{"disambiguationData":[OSD([sQuery(id+"F3.wireOp",EDGE,"E15.bottom"),sQuery(id+"F3.wireOp",EDGE,"E15.left")])]});
            var Q6;
            Q6=makeQuery(id+"F2.opExtrude","SWEPT_EDGE",EDGE,{"disambiguationData":[OSD([sQuery(id+"F0.wireOp",EDGE,"E12"),sQuery(id+"F0.wireOp",EDGE,"E13")])]});
            var Q7;
            Q7=makeQuery(id+"F4.opExtrude","SWEPT_EDGE",EDGE,{"disambiguationData":[OSD([sQuery(id+"F3.wireOp",EDGE,"E15.bottom"),sQuery(id+"F3.wireOp",EDGE,"E15.right")])]});
            chamfer(context, id + "F15", {"entities" : qUnion([Q0, Q1, Q2, Q3, Q4, Q5, Q6, Q7]), "width" : .4 * mm, "tangentPropagation" : true});
        }
        {
            var Q0;
            Q0=qCreatedBy(makeId("Top.planeOp"),FACE);
            cPlane(context, id + "F16", {"entities" : qUnion([Q0]), "cplaneType" : CPlaneType.OFFSET, "offset" : 40 * mm, "width" : 150 * mm, "height" : 150 * mm});
        }
        {
            var Q0;
            Q0=qCreatedBy(id+"F16.planeOp",FACE);
            var sketch = newSketch(context, id + "F17", { "sketchPlane" : qUnion([Q0])});
            skArc(sketch, "E33", {"start": v(-37.6, -16.43) * mm, "mid": v(41.03, 0) * mm, "end": v(-37.6, 16.43) * mm});
            skCircle(sketch, "E34", {"center": v(0, 0) * mm, "radius": 34 * mm});
            skLineSegment(sketch, "E35.bottom", {"start": v(3, 33.87) * mm, "end": v(-3, 33.87) * mm});
            skLineSegment(sketch, "E35.top", {"start": v(3, 40.92) * mm, "end": v(-3, 40.92) * mm});
            skLineSegment(sketch, "E35.left", {"start": v(3, 33.87) * mm, "end": v(3, 40.92) * mm});
            skLineSegment(sketch, "E35.right", {"start": v(-3, 33.87) * mm, "end": v(-3, 40.92) * mm});
            skPoint(sketch, "E35.middle", {"position": v(0, 37.4) * mm});
            skLineSegment(sketch, "E36.bottom", {"start": v(3, -40.92) * mm, "end": v(-3, -40.92) * mm});
            skLineSegment(sketch, "E36.top", {"start": v(3, -33.87) * mm, "end": v(-3, -33.87) * mm});
            skLineSegment(sketch, "E36.left", {"start": v(3, -40.92) * mm, "end": v(3, -33.87) * mm});
            skLineSegment(sketch, "E36.right", {"start": v(-3, -40.92) * mm, "end": v(-3, -33.87) * mm});
            skPoint(sketch, "E36.middle", {"position": v(0, -37.4) * mm});
            skLineSegment(sketch, "E37.bottom", {"start": v(40.92, -3) * mm, "end": v(33.87, -3) * mm});
            skLineSegment(sketch, "E37.top", {"start": v(40.92, 3) * mm, "end": v(33.87, 3) * mm});
            skLineSegment(sketch, "E37.left", {"start": v(40.92, -3) * mm, "end": v(40.92, 3) * mm});
            skLineSegment(sketch, "E37.right", {"start": v(33.87, -3) * mm, "end": v(33.87, 3) * mm});
            skPoint(sketch, "E37.middle", {"position": v(37.4, 0) * mm});
            skSolve(sketch);
        }
        {
            var Q0;
            Q0=makeQuery(id+"F17.imprint","IMPRINT",FACE,{"disambiguationData":[TD([[makeQuery(id+"F17.imprint","IMPRINT",EDGE,{"derivedFrom":sQuery(id+"F17.wireOp",EDGE,"E35.top")}),1.0]])]});
            var Q1;
            {var subQ1=sQuery(id+"F17.wireOp",EDGE,"E37.bottom");Q1=makeQuery(id+"F17.imprint","IMPRINT",FACE,{"disambiguationData":[TD([[makeQuery(id+"F17.imprint","IMPRINT",EDGE,{"derivedFrom":subQ1}),-1.0]])]});}
            var Q2;
            Q2=makeQuery(id+"F17.imprint","IMPRINT",FACE,{"disambiguationData":[TD([[makeQuery(id+"F17.imprint","IMPRINT",EDGE,{"derivedFrom":sQuery(id+"F17.wireOp",EDGE,"E36.bottom")}),-1.0]])]});
            extrude(context, id + "F18", {"entities" : qUnion([Q0, Q1, Q2]), "operationType" : NewBodyOperationType.ADD, "depth" : 20 * mm, "offsetDistance" : 25 * mm});
        }
        {
            var Q0;
            Q0=makeQuery(id+"F18.opExtrude","CAP_FACE",FACE,{"disambiguationData":[OSD([sQuery(id+"F17.wireOp",EDGE,"E34"),sQuery(id+"F17.wireOp",EDGE,"E37.bottom"),sQuery(id+"F17.wireOp",EDGE,"E37.top"),sQuery(id+"F17.wireOp",EDGE,"E37.left")])],"isStart":false});
            var sketch = newSketch(context, id + "F19", { "sketchPlane" : qUnion([Q0])});
            skPoint(sketch, "E38", {"position": v(37.4, 0) * mm});
            skPoint(sketch, "E38.positionSnap0", {"position": v(37.4, -3) * mm});
            skPoint(sketch, "E38.positionSnap1", {"position": v(40.92, 0) * mm});
            skSolve(sketch);
        }
        {
            var Q0;
            Q0=makeQuery(id+"F18.opExtrude","CAP_FACE",FACE,{"disambiguationData":[OSD([sQuery(id+"F17.wireOp",EDGE,"E34"),sQuery(id+"F17.wireOp",EDGE,"E35.top"),sQuery(id+"F17.wireOp",EDGE,"E35.left"),sQuery(id+"F17.wireOp",EDGE,"E35.right")])],"isStart":false});
            var sketch = newSketch(context, id + "F20", { "sketchPlane" : qUnion([Q0])});
            skPoint(sketch, "E39", {"position": v(0, 37.4) * mm});
            skPoint(sketch, "E39.positionSnap0", {"position": v(0, 40.92) * mm});
            skPoint(sketch, "E39.positionSnap1", {"position": v(3, 37.4) * mm});
            skSolve(sketch);
        }
        {
            var Q0;
            Q0=makeQuery(id+"F18.opExtrude","CAP_FACE",FACE,{"disambiguationData":[OSD([sQuery(id+"F17.wireOp",EDGE,"E34"),sQuery(id+"F17.wireOp",EDGE,"E36.bottom"),sQuery(id+"F17.wireOp",EDGE,"E36.left"),sQuery(id+"F17.wireOp",EDGE,"E36.right")])],"isStart":false});
            var sketch = newSketch(context, id + "F21", { "sketchPlane" : qUnion([Q0])});
            skPoint(sketch, "E40", {"position": v(0, -37.4) * mm});
            skPoint(sketch, "E40.positionSnap0", {"position": v(0, -40.92) * mm});
            skPoint(sketch, "E40.positionSnap1", {"position": v(3, -37.4) * mm});
            skSolve(sketch);
        }
        {
            var Q0;
            Q0=sQuery(id+"F20.wireOp",VERTEX,"E39");
            var Q1;
            Q1=sQuery(id+"F19.wireOp",VERTEX,"E38");
            var Q2;
            Q2=sQuery(id+"F21.wireOp",VERTEX,"E40");
            var Q3;
            Q3=makeQuery(id+"F1.opRevolve","SWEPT_BODY",BODY,{"disambiguationData":[OSD([sQuery(id+"F0.wireOp",EDGE,"E0"),sQuery(id+"F0.wireOp",EDGE,"E2.0"),sQuery(id+"F0.wireOp",EDGE,"E4"),sQuery(id+"F0.wireOp",EDGE,"E11.left")])]});
            hole(context, id + "F22", {"style" : HoleStyle.SIMPLE, "endStyle" : HoleEndStyle.BLIND, "holeDiameter" : 3.16 * mm, "holeDepth" : 15 * mm, "isTappedThrough" : true, "tappedDepth" : 12 * mm, "tapClearance" : 3, "locations" : qUnion([Q0, Q1, Q2]), "scope" : qUnion([Q3])});
        }
        {
            var Q0;
            Q0=makeQuery(id+"F18.boolean.opBoolean","INTERSECT",EDGE,{"derivedFrom":[makeQuery(id+"F1.opRevolve","SWEPT_FACE",FACE,{"disambiguationData":[OSD([sQuery(id+"F0.wireOp",EDGE,"E2.0")])]}),makeQuery(id+"F18.opExtrude","SWEPT_FACE",FACE,{"disambiguationData":[OSD([sQuery(id+"F17.wireOp",EDGE,"E36.bottom")])]})]});
            var Q1;
            Q1=makeQuery(id+"F18.boolean.opBoolean","INTERSECT",EDGE,{"derivedFrom":[makeQuery(id+"F1.opRevolve","SWEPT_FACE",FACE,{"disambiguationData":[OSD([sQuery(id+"F0.wireOp",EDGE,"E2.0")])]}),makeQuery(id+"F18.opExtrude","SWEPT_FACE",FACE,{"disambiguationData":[OSD([sQuery(id+"F17.wireOp",EDGE,"E37.left")])]})]});
            var Q2;
            Q2=makeQuery(id+"F18.boolean.opBoolean","INTERSECT",EDGE,{"derivedFrom":[makeQuery(id+"F1.opRevolve","SWEPT_FACE",FACE,{"disambiguationData":[OSD([sQuery(id+"F0.wireOp",EDGE,"E2.0")])]}),makeQuery(id+"F18.opExtrude","SWEPT_FACE",FACE,{"disambiguationData":[OSD([sQuery(id+"F17.wireOp",EDGE,"E35.top")])]})]});
            var Q3;
            {var subQ0=sQuery(id+"F17.wireOp",EDGE,"E35.bottom");var subQ1=sQuery(id+"F17.wireOp",EDGE,"E34");Q3=makeQuery(id+"F18.boolean.opBoolean","INTERSECT",EDGE,{"derivedFrom":[makeQuery(id+"F1.opRevolve","SWEPT_FACE",FACE,{"disambiguationData":[OSD([sQuery(id+"F0.wireOp",EDGE,"E2.0")])]}),makeQuery(id+"F18.opExtrude","SWEPT_FACE",FACE,{"disambiguationData":[OSD([subQ1]),TDD([makeQuery(id+"F17.imprint","IMPRINT",EDGE,{"disambiguationData":[TD([[makeQuery(id+"F17.imprint","INTERSECT",VERTEX,{"derivedFrom":[subQ1,subQ0,sQuery(id+"F17.wireOp",EDGE,"E35.left")]}),-1.0]])],"derivedFrom":subQ1})])]})]});}
            var Q4;
            {var subQ0=sQuery(id+"F17.wireOp",EDGE,"E36.top");var subQ1=sQuery(id+"F17.wireOp",EDGE,"E34");Q4=makeQuery(id+"F18.boolean.opBoolean","INTERSECT",EDGE,{"derivedFrom":[makeQuery(id+"F1.opRevolve","SWEPT_FACE",FACE,{"disambiguationData":[OSD([sQuery(id+"F0.wireOp",EDGE,"E2.0")])]}),makeQuery(id+"F18.opExtrude","SWEPT_FACE",FACE,{"disambiguationData":[OSD([subQ1]),TDD([makeQuery(id+"F17.imprint","IMPRINT",EDGE,{"disambiguationData":[TD([[makeQuery(id+"F17.imprint","INTERSECT",VERTEX,{"derivedFrom":[subQ1,subQ0,sQuery(id+"F17.wireOp",EDGE,"E36.left")]}),1.0]])],"derivedFrom":subQ1})])]})]});}
            var Q5;
            {var subQ0=sQuery(id+"F17.wireOp",EDGE,"E37.right");var subQ1=sQuery(id+"F17.wireOp",EDGE,"E34");Q5=makeQuery(id+"F18.boolean.opBoolean","INTERSECT",EDGE,{"derivedFrom":[makeQuery(id+"F1.opRevolve","SWEPT_FACE",FACE,{"disambiguationData":[OSD([sQuery(id+"F0.wireOp",EDGE,"E2.0")])]}),makeQuery(id+"F18.opExtrude","SWEPT_FACE",FACE,{"disambiguationData":[OSD([subQ1]),TDD([makeQuery(id+"F17.imprint","IMPRINT",EDGE,{"disambiguationData":[TD([[makeQuery(id+"F17.imprint","INTERSECT",VERTEX,{"derivedFrom":[subQ1,sQuery(id+"F17.wireOp",EDGE,"E37.bottom"),subQ0]}),-1.0]])],"derivedFrom":subQ1})])]})]});}
            fillet(context, id + "F23", {"entities" : qUnion([Q0, Q1, Q2, Q3, Q4, Q5]), "radius" : 5 * mm, "tangentPropagation" : true, "allowEdgeOverflow" : false});
        }
        {
            var Q0;
            Q0=makeQuery(id+"F18.boolean.opBoolean","INTERSECT",EDGE,{"derivedFrom":[makeQuery(id+"F1.opRevolve","SWEPT_FACE",FACE,{"disambiguationData":[OSD([sQuery(id+"F0.wireOp",EDGE,"E2.0")])]}),makeQuery(id+"F18.opExtrude","SWEPT_FACE",FACE,{"disambiguationData":[OSD([sQuery(id+"F17.wireOp",EDGE,"E36.right")])]})]});
            var Q1;
            Q1=makeQuery(id+"F18.boolean.opBoolean","INTERSECT",EDGE,{"derivedFrom":[makeQuery(id+"F1.opRevolve","SWEPT_FACE",FACE,{"disambiguationData":[OSD([sQuery(id+"F0.wireOp",EDGE,"E2.0")])]}),makeQuery(id+"F18.opExtrude","SWEPT_FACE",FACE,{"disambiguationData":[OSD([sQuery(id+"F17.wireOp",EDGE,"E36.left")])]})]});
            var Q2;
            Q2=makeQuery(id+"F18.boolean.opBoolean","INTERSECT",EDGE,{"derivedFrom":[makeQuery(id+"F1.opRevolve","SWEPT_FACE",FACE,{"disambiguationData":[OSD([sQuery(id+"F0.wireOp",EDGE,"E2.0")])]}),makeQuery(id+"F18.opExtrude","SWEPT_FACE",FACE,{"disambiguationData":[OSD([sQuery(id+"F17.wireOp",EDGE,"E37.bottom")])]})]});
            var Q3;
            Q3=makeQuery(id+"F18.boolean.opBoolean","INTERSECT",EDGE,{"derivedFrom":[makeQuery(id+"F1.opRevolve","SWEPT_FACE",FACE,{"disambiguationData":[OSD([sQuery(id+"F0.wireOp",EDGE,"E2.0")])]}),makeQuery(id+"F18.opExtrude","SWEPT_FACE",FACE,{"disambiguationData":[OSD([sQuery(id+"F17.wireOp",EDGE,"E37.top")])]})]});
            var Q4;
            Q4=makeQuery(id+"F18.boolean.opBoolean","INTERSECT",EDGE,{"derivedFrom":[makeQuery(id+"F1.opRevolve","SWEPT_FACE",FACE,{"disambiguationData":[OSD([sQuery(id+"F0.wireOp",EDGE,"E2.0")])]}),makeQuery(id+"F18.opExtrude","SWEPT_FACE",FACE,{"disambiguationData":[OSD([sQuery(id+"F17.wireOp",EDGE,"E35.left")])]})]});
            var Q5;
            Q5=makeQuery(id+"F18.boolean.opBoolean","INTERSECT",EDGE,{"derivedFrom":[makeQuery(id+"F1.opRevolve","SWEPT_FACE",FACE,{"disambiguationData":[OSD([sQuery(id+"F0.wireOp",EDGE,"E2.0")])]}),makeQuery(id+"F18.opExtrude","SWEPT_FACE",FACE,{"disambiguationData":[OSD([sQuery(id+"F17.wireOp",EDGE,"E35.right")])]})]});
            fillet(context, id + "F24", {"entities" : qUnion([Q0, Q1, Q2, Q3, Q4, Q5]), "radius" : 1 * mm, "tangentPropagation" : true, "allowEdgeOverflow" : false});
        }
    });
